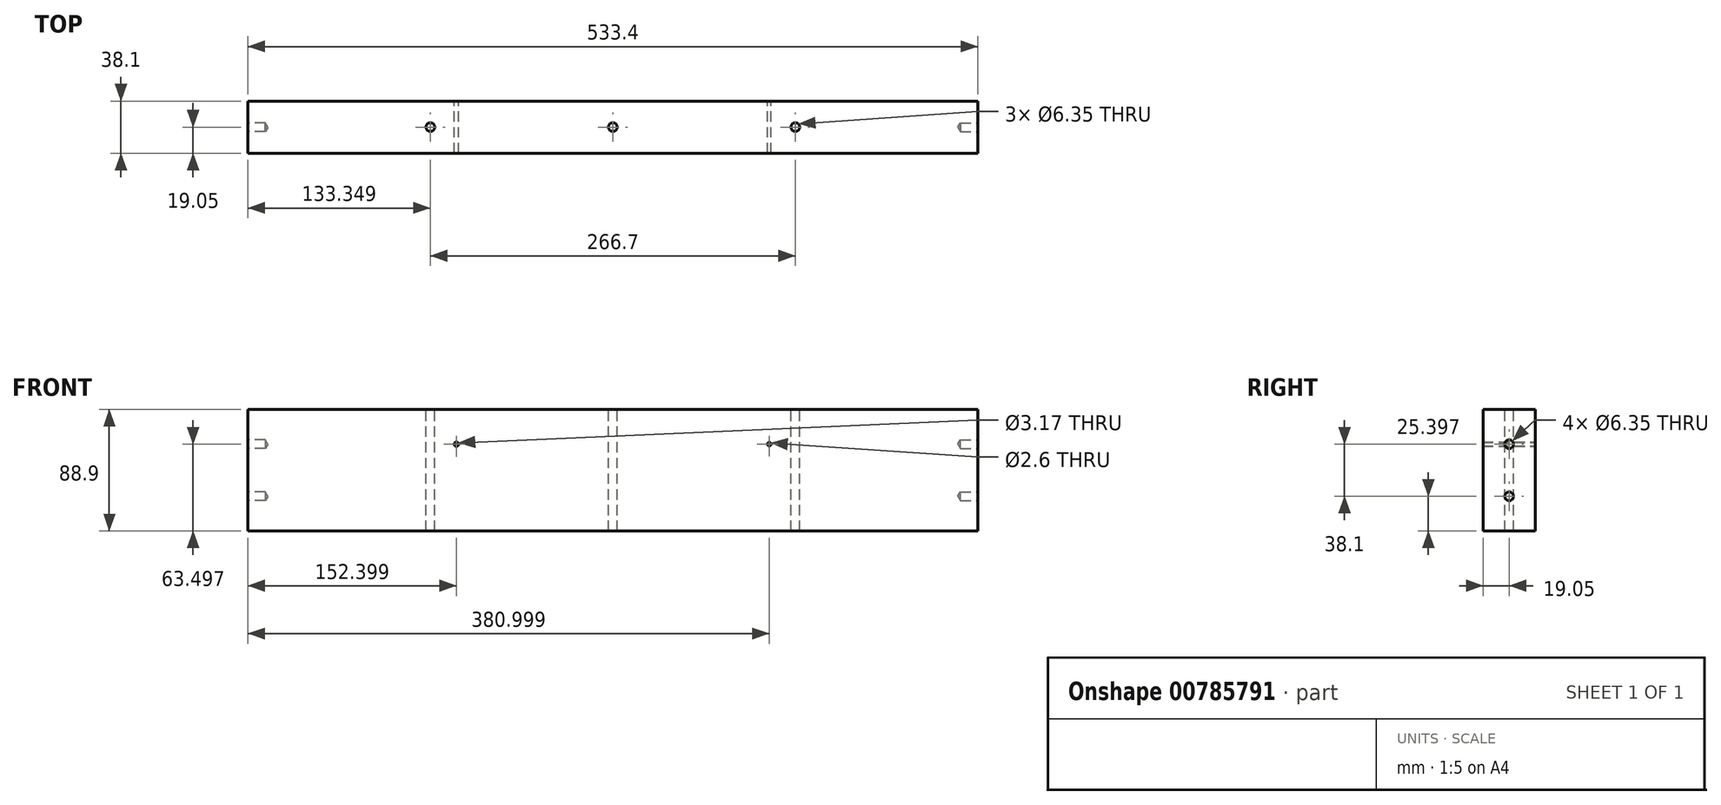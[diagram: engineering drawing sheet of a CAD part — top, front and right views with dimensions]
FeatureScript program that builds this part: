
annotation { "Feature Type Name" : "Feature", "Feature Type Description" : "" }
export const myFeature = defineFeature(function(context is Context, id is Id, definition is map)
    precondition{}
    {
        {
            var Q0;
            Q0=qCreatedBy(makeId("Front.planeOp"),FACE);
            var sketch = newSketch(context, id + "F0", { "sketchPlane" : qUnion([Q0])});
            skLineSegment(sketch, "E0.bottom", {"start": v(-145.95, -4.54) * mm, "end": v(387.45, -4.54) * mm});
            skLineSegment(sketch, "E0.top", {"start": v(-145.95, -93.44) * mm, "end": v(387.45, -93.44) * mm});
            skLineSegment(sketch, "E0.left", {"start": v(-145.95, -4.54) * mm, "end": v(-145.95, -93.44) * mm});
            skLineSegment(sketch, "E0.right", {"start": v(387.45, -4.54) * mm, "end": v(387.45, -93.44) * mm});
            skSolve(sketch);
        }
        {
            var Q0;
            Q0=makeQuery(id+"F0.imprint","IMPRINT",FACE,{"disambiguationData":[TD([[makeQuery(id+"F0.imprint","IMPRINT",EDGE,{"derivedFrom":sQuery(id+"F0.wireOp",EDGE,"E0.bottom")}),-1.0]])]});
            extrude(context, id + "F1", {"entities" : qUnion([Q0]), "depth" : 38.1 * mm, "offsetDistance" : 25.4 * mm});
        }
        {
            var Q0;
            Q0=makeQuery(id+"F1.opExtrude","SWEPT_FACE",FACE,{"disambiguationData":[OSD([sQuery(id+"F0.wireOp",EDGE,"E0.right")])]});
            var sketch = newSketch(context, id + "F2", { "sketchPlane" : qUnion([Q0])});
            skLineSegment(sketch, "E1", {"start": v(-19.05, -4.54) * mm, "end": v(-19.05, -93.44) * mm, "construction": true});
            skPoint(sketch, "E2", {"position": v(-19.05, -29.94) * mm});
            skPoint(sketch, "E3", {"position": v(-19.05, -68.04) * mm});
            skSolve(sketch);
        }
        {
            var Q0;
            Q0=sQuery(id+"F2.wireOp",VERTEX,"E2");
            var Q1;
            Q1=sQuery(id+"F2.wireOp",VERTEX,"E3");
            var Q2;
            Q2=makeQuery(id+"F1.opExtrude","SWEPT_BODY",BODY,{"disambiguationData":[OSD([sQuery(id+"F0.wireOp",EDGE,"E0.bottom"),sQuery(id+"F0.wireOp",EDGE,"E0.top"),sQuery(id+"F0.wireOp",EDGE,"E0.left"),sQuery(id+"F0.wireOp",EDGE,"E0.right")])]});
            hole(context, id + "F3", {"style" : HoleStyle.SIMPLE, "endStyle" : HoleEndStyle.BLIND, "holeDiameter" : 6.35 * mm, "majorDiameter" : 6.35 * mm, "holeDepth" : 12.7 * mm, "isTappedThrough" : true, "tappedDepth" : 12.7 * mm, "tapClearance" : 3, "locations" : qUnion([Q0, Q1]), "scope" : qUnion([Q2])});
        }
        {
            var Q0;
            Q0=makeQuery(id+"F1.opExtrude","SWEPT_FACE",FACE,{"disambiguationData":[OSD([sQuery(id+"F0.wireOp",EDGE,"E0.left")])]});
            var sketch = newSketch(context, id + "F4", { "sketchPlane" : qUnion([Q0])});
            skLineSegment(sketch, "E4", {"start": v(19.05, -4.54) * mm, "end": v(19.05, -93.44) * mm, "construction": true});
            skPoint(sketch, "E5", {"position": v(19.05, -29.94) * mm});
            skPoint(sketch, "E6", {"position": v(19.05, -68.04) * mm});
            skSolve(sketch);
        }
        {
            var Q0;
            Q0=sQuery(id+"F4.wireOp",VERTEX,"E5");
            var Q1;
            Q1=sQuery(id+"F4.wireOp",VERTEX,"E6");
            var Q2;
            Q2=makeQuery(id+"F1.opExtrude","SWEPT_BODY",BODY,{"disambiguationData":[OSD([sQuery(id+"F0.wireOp",EDGE,"E0.bottom"),sQuery(id+"F0.wireOp",EDGE,"E0.top"),sQuery(id+"F0.wireOp",EDGE,"E0.left"),sQuery(id+"F0.wireOp",EDGE,"E0.right")])]});
            hole(context, id + "F5", {"style" : HoleStyle.SIMPLE, "endStyle" : HoleEndStyle.BLIND, "holeDiameter" : 6.35 * mm, "majorDiameter" : 6.35 * mm, "holeDepth" : 12.7 * mm, "isTappedThrough" : true, "tappedDepth" : 12.7 * mm, "tapClearance" : 3, "locations" : qUnion([Q0, Q1]), "scope" : qUnion([Q2])});
        }
        {
            var Q0;
            Q0=makeQuery(id+"F1.opExtrude","SWEPT_FACE",FACE,{"disambiguationData":[OSD([sQuery(id+"F0.wireOp",EDGE,"E0.bottom")])]});
            var sketch = newSketch(context, id + "F6", { "sketchPlane" : qUnion([Q0])});
            skLineSegment(sketch, "E7", {"start": v(-145.95, -19.05) * mm, "end": v(387.45, -19.05) * mm, "construction": true});
            skPoint(sketch, "E8", {"position": v(-12.6, -19.05) * mm});
            skPoint(sketch, "E9", {"position": v(120.75, -19.05) * mm});
            skPoint(sketch, "E10", {"position": v(254.1, -19.05) * mm});
            skSolve(sketch);
        }
        {
            var Q0;
            Q0=sQuery(id+"F6.wireOp",VERTEX,"E8");
            var Q1;
            Q1=sQuery(id+"F6.wireOp",VERTEX,"E9");
            var Q2;
            Q2=sQuery(id+"F6.wireOp",VERTEX,"E10");
            var Q3;
            Q3=makeQuery(id+"F1.opExtrude","SWEPT_BODY",BODY,{"disambiguationData":[OSD([sQuery(id+"F0.wireOp",EDGE,"E0.bottom"),sQuery(id+"F0.wireOp",EDGE,"E0.top"),sQuery(id+"F0.wireOp",EDGE,"E0.left"),sQuery(id+"F0.wireOp",EDGE,"E0.right")])]});
            hole(context, id + "F7", {"style" : HoleStyle.SIMPLE, "endStyle" : HoleEndStyle.THROUGH, "holeDiameter" : 6.35 * mm, "majorDiameter" : 6.35 * mm, "isTappedThrough" : true, "tappedDepth" : 12.7 * mm, "tapClearance" : 3, "locations" : qUnion([Q0, Q1, Q2]), "scope" : qUnion([Q3])});
        }
        {
            var Q0;
            Q0=makeQuery(id+"F1.opExtrude","CAP_FACE",FACE,{"disambiguationData":[OSD([sQuery(id+"F0.wireOp",EDGE,"E0.bottom"),sQuery(id+"F0.wireOp",EDGE,"E0.top"),sQuery(id+"F0.wireOp",EDGE,"E0.left"),sQuery(id+"F0.wireOp",EDGE,"E0.right")])],"isStart":true});
            var sketch = newSketch(context, id + "F8", { "sketchPlane" : qUnion([Q0])});
            skCircle(sketch, "E11", {"center": v(-235.05, -29.94) * mm, "radius": 1.3 * mm});
            skCircle(sketch, "E12", {"center": v(-6.45, -29.94) * mm, "radius": 1.59 * mm});
            skLineSegment(sketch, "E13", {"start": v(145.95, -29.94) * mm, "end": v(-387.45, -29.94) * mm, "construction": true});
            skSolve(sketch);
        }
        {
            var Q0;
            Q0=makeQuery(id+"F8.imprint","IMPRINT",FACE,{"disambiguationData":[TD([[makeQuery(id+"F8.imprint","IMPRINT",EDGE,{"derivedFrom":sQuery(id+"F8.wireOp",EDGE,"E11")}),1.0]])]});
            var Q1;
            Q1=makeQuery(id+"F8.imprint","IMPRINT",FACE,{"disambiguationData":[TD([[makeQuery(id+"F8.imprint","IMPRINT",EDGE,{"derivedFrom":sQuery(id+"F8.wireOp",EDGE,"E12")}),1.0]])]});
            extrude(context, id + "F9", {"entities" : qUnion([Q0, Q1]), "operationType" : NewBodyOperationType.REMOVE, "endBound" : BoundingType.THROUGH_ALL, "oppositeDirection" : true, "depth" : 25.4 * mm, "offsetDistance" : 25.4 * mm});
        }
    });
